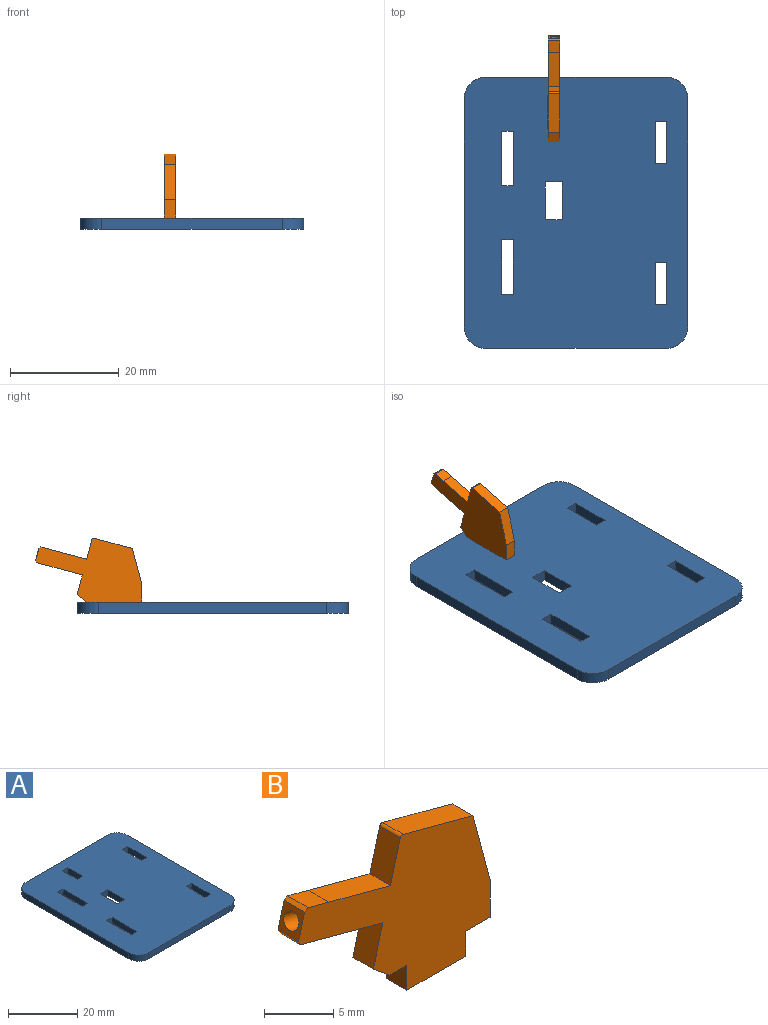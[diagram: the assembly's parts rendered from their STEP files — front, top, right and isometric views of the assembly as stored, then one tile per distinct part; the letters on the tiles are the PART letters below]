
ASSEMBLY  parts=2 mates=1
PART A: 34 faces, bbox 41.3x50x2.1 mm
  f0: plane 2.2x2.1mm, normal (0,1,0), area 4.6mm2, adj f1,f31,f32,f33
  f1: plane 10x2.1mm, normal (1,0,0), area 21mm2, adj f0,f2,f32,f33
  f2: plane 2.2x2.1mm, normal (0,-1,0), area 4.6mm2, adj f1,f31,f32,f33
  f3: plane 3.1x2.1mm, normal (0,1,0), area 6.5mm2, adj f4,f25,f32,f33
  f4: plane 7x2.1mm, normal (1,0,0), area 14.7mm2, adj f3,f5,f32,f33
  f5: plane 3.1x2.1mm, normal (0,-1,0), area 6.5mm2, adj f4,f25,f32,f33
  f6: plane 2.15x2.1mm, normal (0,-1,0), area 4.5mm2, adj f7,f26,f32,f33
  f7: plane 7.7x2.1mm, normal (-1,0,0), area 16.2mm2, adj f6,f8,f32,f33
  f8: plane 2.15x2.1mm, normal (0,1,0), area 4.5mm2, adj f7,f26,f32,f33
  f9: plane 2.15x2.1mm, normal (0,-1,0), area 4.5mm2, adj f10,f27,f32,f33
  f10: plane 7.7x2.1mm, normal (-1,0,0), area 16.2mm2, adj f9,f11,f32,f33
  f11: plane 2.15x2.1mm, normal (0,1,0), area 4.5mm2, adj f10,f27,f32,f33
  f12: cylinder r=4mm len=4mm, axis (0,0,-1), area 13.2mm2, adj f13,f28,f32,f33
  f13: plane 33.25x2.1mm, normal (0,1,0), area 69.8mm2, adj f12,f14,f32,f33
  f14: cylinder r=4mm len=4mm, axis (0,0,-1), area 13.2mm2, adj f13,f15,f32,f33
  f15: plane 42x2.1mm, normal (-1,0,0), area 88.2mm2, adj f14,f16,f32,f33
  f16: cylinder r=4mm len=4mm, axis (0,0,-1), area 13.2mm2, adj f15,f17,f32,f33
  f17: plane 33.25x2.1mm, normal (0,-1,0), area 69.8mm2, adj f16,f18,f32,f33
  f18: cylinder r=4mm len=4mm, axis (0,0,-1), area 13.2mm2, adj f17,f28,f32,f33
  f19: plane 10x2.1mm, normal (1,0,0), area 21mm2, adj f20,f29,f32,f33
  f20: plane 2.2x2.1mm, normal (0,-1,0), area 4.6mm2, adj f19,f21,f32,f33
  f21: plane 10x2.1mm, normal (-1,0,0), area 21mm2, adj f20,f29,f32,f33
  f22: plane 2.2x2.1mm, normal (0,-1,0), area 4.6mm2, adj f23,f30,f32,f33
  f23: plane 6x2.1mm, normal (-1,0,0), area 12.6mm2, adj f22,f24,f32,f33
  f24: plane 2.2x2.1mm, normal (0,1,0), area 4.6mm2, adj f23,f30,f32,f33
  f25: plane 7x2.1mm, normal (-1,0,0), area 14.7mm2, adj f3,f5,f32,f33
  f26: plane 7.7x2.1mm, normal (1,0,0), area 16.2mm2, adj f6,f8,f32,f33
  f27: plane 7.7x2.1mm, normal (1,0,0), area 16.2mm2, adj f9,f11,f32,f33
  f28: plane 42x2.1mm, normal (1,0,0), area 88.2mm2, adj f12,f18,f32,f33
  f29: plane 2.2x2.1mm, normal (0,1,0), area 4.6mm2, adj f19,f21,f32,f33
  f30: plane 6x2.1mm, normal (1,0,0), area 12.6mm2, adj f22,f24,f32,f33
  f31: plane 10x2.1mm, normal (-1,0,0), area 21mm2, adj f0,f2,f32,f33
  f32: plane 50x41.25mm, normal (0,0,1), area 1936.8mm2, adj f0,f1,f2,f3,f4,f5,f6,f7
  f33: plane 50x41.25mm, normal (0,0,-1), area 1936.8mm2, adj f0,f1,f2,f3,f4,f5,f6,f7
PART B: 24 faces, bbox 19.6x2.1x14 mm
  f0: plane 2.1x1.75mm, normal (0,0,-1), area 3.7mm2, adj f1,f17,f18,f19
  f1: plane 2.2x2.1mm, normal (-1,0,0), area 4.6mm2, adj f0,f2,f18,f19
  f2: plane 6x2.1mm, normal (0,0,-1), area 12.6mm2, adj f1,f3,f18,f19
  f3: plane 2.2x2.1mm, normal (1,0,0), area 4.6mm2, adj f2,f4,f18,f19
  f4: plane 2.5x2.1mm, normal (0,0,-1), area 5.2mm2, adj f3,f5,f18,f19
  f5: plane 3.33x2.1mm, normal (1,0,0), area 7mm2, adj f4,f6,f18,f19
  f6: plane 6.54x2.1mm, normal (0.97,0,0.26), area 14.2mm2, adj f5,f7,f18,f19
  f7: plane 7.12x2.1mm, normal (0.26,0,0.97), area 15.5mm2, adj f6,f8,f18,f19
  f8: cylinder r=0.25mm len=2.1mm, axis (0,1,0), area 0.8mm2, adj f7,f9,f18,f19
  f9: plane 3.71x2.1mm, normal (-0.97,0,0.26), area 8.1mm2, adj f8,f10,f18,f19
  f10: plane 6.29x2.1mm, normal (0.26,0,0.97), area 13.7mm2, adj f9,f11,f18,f19
  f11: plane 2.11x2.1mm, normal (0.26,0,0.97), area 4.6mm2, adj f10,f12,f18,f19
  f12: plane 2.1x0.37mm, normal (-0.5,0,0.87), area 0.9mm2, adj f11,f13,f18,f19
  f13: plane 2.32x2.1mm, normal (-0.97,0,0.26), area 3.3mm2, adj f12,f14,f18,f19,f20
  f14: plane 2.1x0.37mm, normal (-0.87,0,-0.5), area 0.9mm2, adj f13,f15,f18,f19
  f15: plane 8.4x2.25mm, normal (-0.26,0,-0.97), area 18.3mm2, adj f14,f16,f18,f19
  f16: plane 3.62x2.1mm, normal (-0.97,0,0.26), area 7.9mm2, adj f15,f17,f18,f19
  f17: plane 2.1x1.68mm, normal (-0.63,0,-0.77), area 4.6mm2, adj f0,f16,f18,f19
  f18: plane 19.57x13.99mm, normal (0,-1,0), area 149mm2, adj f0,f1,f2,f3,f4,f5,f6,f7
  f19: plane 19.57x13.99mm, normal (0,1,0), area 149mm2, adj f0,f1,f2,f3,f4,f5,f6,f7
  f20: cylinder r=0.75mm len=1.84mm, axis (-0.97,0,0.26), area 7.1mm2, adj f13,f21
  f21: cone r=0mm half-angle=59deg, axis (-0.97,0,0.26), area 1.1mm2, adj f20,f23
  f22: cone r=0mm half-angle=59deg, axis (-0.97,0,0.26), area 0.9mm2, adj f23
  f23: cylinder r=0.5mm len=1.56mm, axis (-0.97,0,0.26), area 4.2mm2, adj f21,f22
PLACE A t=(88.6,-41.69,-19.61)mm
PLACE B rot(axis=(0,0,-1),90deg) t=(-115.57,-52.24,54.06)mm
MATE fastened B.f0 <-> A.f32  axis (0,0,-1) through (-115.57,6.79,48.82)mm
